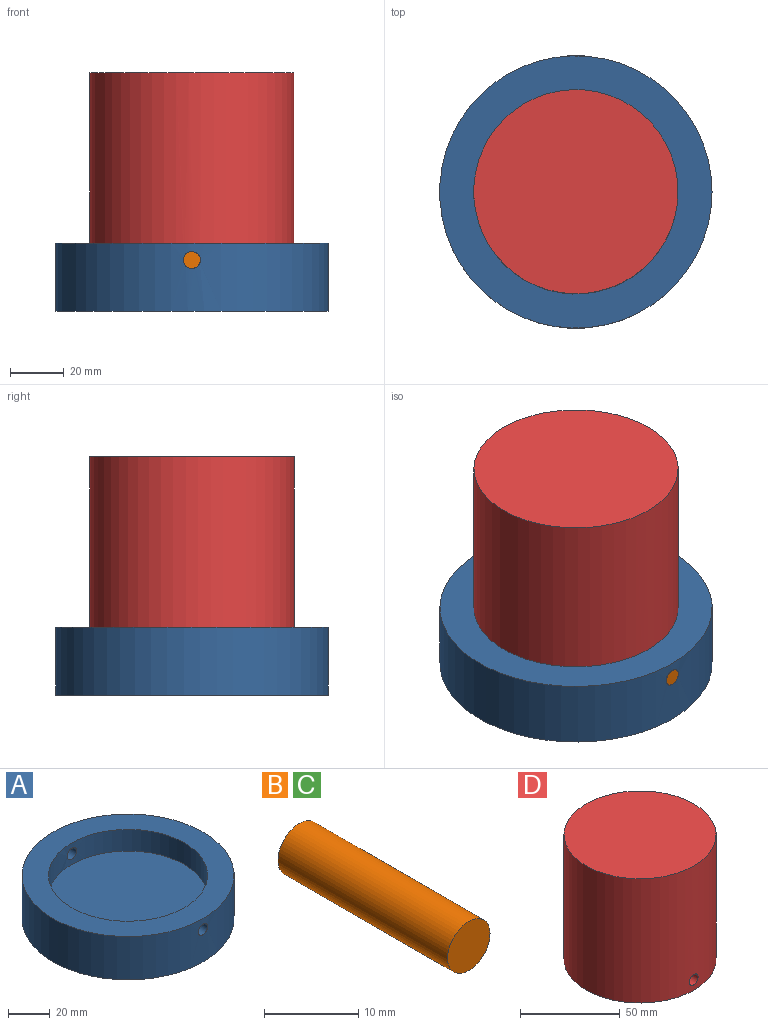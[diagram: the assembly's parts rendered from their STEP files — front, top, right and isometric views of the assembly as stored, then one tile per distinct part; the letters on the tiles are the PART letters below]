
ASSEMBLY  parts=4 mates=4
PART A: 7 faces, bbox 101.6x101.6x25.4 mm
  f0: cylinder r=50.8mm len=101.6mm, axis (0,0,-1), area 8043.8mm2, adj f2,f3,f5,f6
  f1: cylinder r=38.1mm len=76.2mm, axis (0,0,1), area 2976.7mm2, adj f2,f4,f5,f6
  f2: plane 101.6x101.6mm, normal (0,0,1), area 3547mm2, adj f0,f1
  f3: plane 101.6x101.6mm, normal (0,0,-1), area 8107.3mm2, adj f0
  f4: plane 76.2x76.2mm, normal (0,0,1), area 4560.4mm2, adj f1
  f5: cylinder r=3.17mm len=12.83mm, axis (0,1,0), area 253.7mm2, adj f0,f1
  f6: cylinder r=3.17mm len=12.83mm, axis (0,1,0), area 253.7mm2, adj f0,f1
PART B: 3 faces, bbox 6.4x25.4x6.4 mm
  f0: cylinder r=3.17mm len=25.4mm, axis (0,1,0), area 506.7mm2, adj f1,f2
  f1: plane 6.35x6.35mm, normal (0,-1,0), area 31.7mm2, adj f0
  f2: plane 6.35x6.35mm, normal (0,1,0), area 31.7mm2, adj f0
PART C: same geometry as B
PART D: 4 faces, bbox 76.2x76.2x76.2 mm
  f0: cylinder r=38.1mm len=76.2mm, axis (0,0,-1), area 18177.9mm2, adj f1,f2,f3
  f1: plane 76.2x76.2mm, normal (0,0,1), area 4560.4mm2, adj f0
  f2: plane 76.2x76.2mm, normal (0,0,-1), area 4560.4mm2, adj f0
  f3: cylinder r=3.17mm len=76.2mm, axis (0,1,0), area 1517.5mm2, adj f0
PLACE A rot(axis=(0.39,-0.31,0.87),0deg) t=(1.08,-49.29,-20.44)mm
PLACE B rot(axis=(0.39,-0.31,0.87),0deg) t=(1.08,-74.77,-1.39)mm
PLACE C rot(axis=(0.39,-0.31,0.87),0deg) t=(1.08,1.59,-1.39)mm
PLACE D t=(1.08,-49.29,-20.44)mm
MATE fastened A.f5 <-> B.f0  axis (0,1,0) through (1.08,-100.17,-1.39)mm
MATE slider B.f0 <-> D.f3  axis (0,1,0) through (1.08,-87.47,-1.39)mm
MATE fastened A.f0 <-> D.f0  axis (0,0,1) through (1.08,-49.29,-7.74)mm
MATE fastened C.f0 <-> A.f5  axis (0,1,0) through (1.08,1.59,-1.39)mm
